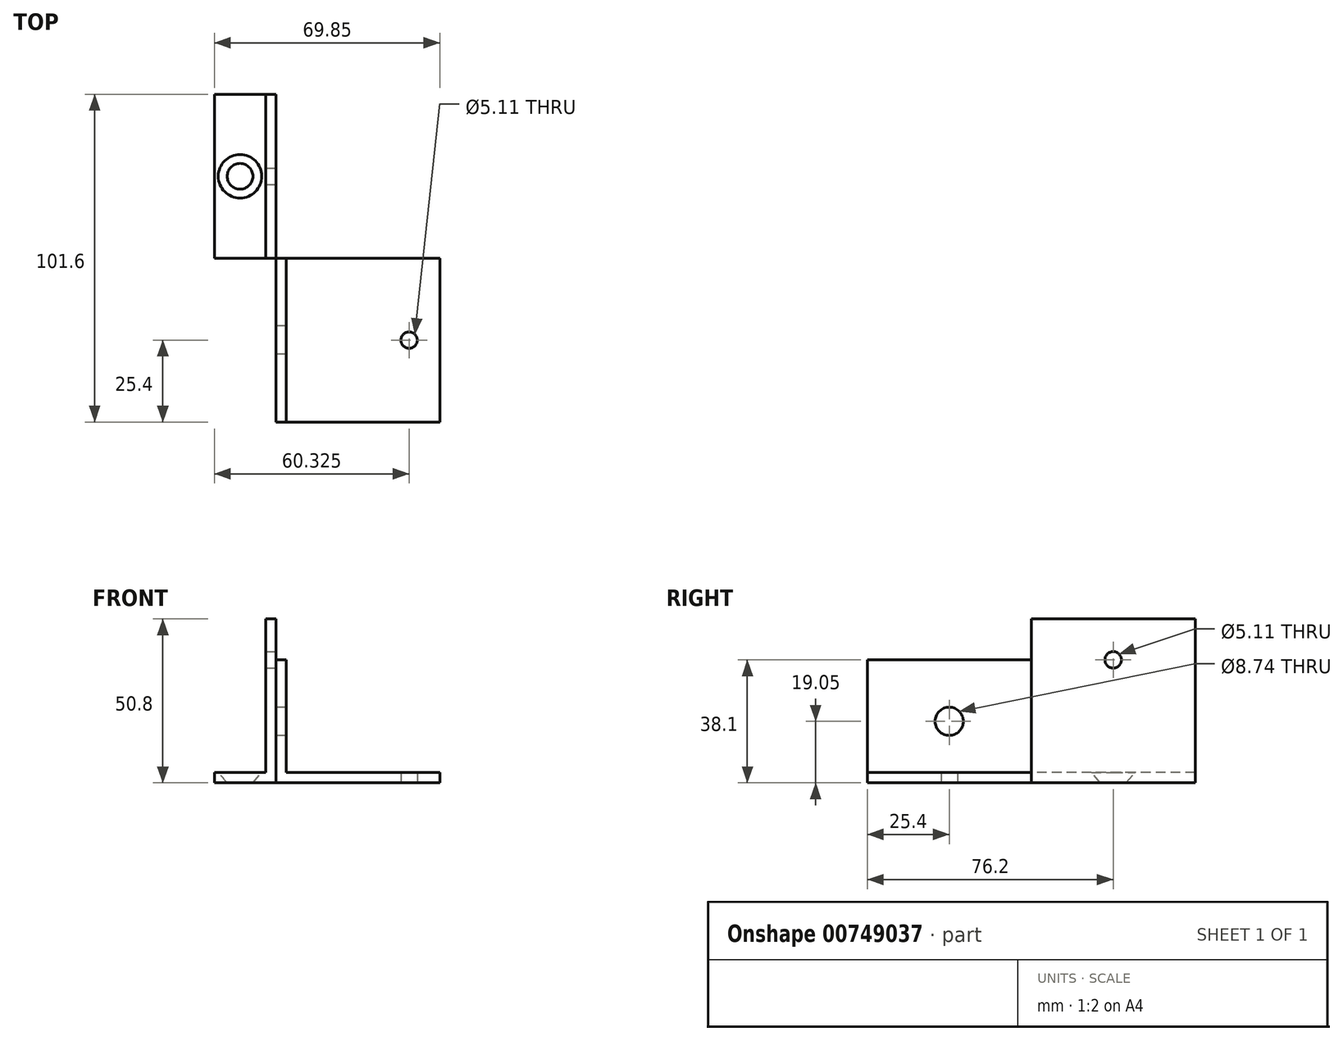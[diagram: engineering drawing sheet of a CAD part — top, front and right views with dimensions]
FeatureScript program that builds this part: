
annotation { "Feature Type Name" : "Feature", "Feature Type Description" : "" }
export const myFeature = defineFeature(function(context is Context, id is Id, definition is map)
    precondition{}
    {
        {
            var Q0;
            Q0=qCreatedBy(makeId("Front.planeOp"),FACE);
            var sketch = newSketch(context, id + "F0", { "sketchPlane" : qUnion([Q0])});
            skLineSegment(sketch, "E0", {"start": v(0, 0) * mm, "end": v(50.8, 0) * mm});
            skLineSegment(sketch, "E1", {"start": v(50.8, 0) * mm, "end": v(50.8, 3.18) * mm});
            skLineSegment(sketch, "E2", {"start": v(50.8, 3.18) * mm, "end": v(3.18, 3.18) * mm});
            skLineSegment(sketch, "E3", {"start": v(3.18, 3.17) * mm, "end": v(3.18, 50.8) * mm});
            skLineSegment(sketch, "E4", {"start": v(3.18, 50.8) * mm, "end": v(0, 50.8) * mm});
            skLineSegment(sketch, "E5", {"start": v(0, 50.8) * mm, "end": v(0, 0) * mm});
            skSolve(sketch);
        }
        {
            var Q0;
            Q0 = qSketchRegion(id + "F0", true);
            extrude(context, id + "F1", {"entities" : qUnion([Q0]), "depth" : 50.8 * mm, "offsetDistance" : 25.4 * mm});
        }
        {
            var Q0;
            Q0=makeQuery(id+"F1.opExtrude","SWEPT_FACE",FACE,{"disambiguationData":[OSD([sQuery(id+"F0.wireOp",EDGE,"E2")])]});
            var sketch = newSketch(context, id + "F2", { "sketchPlane" : qUnion([Q0])});
            skPoint(sketch, "E6", {"position": v(41.28, -25.4) * mm});
            skSolve(sketch);
        }
        {
            var Q0;
            Q0=sQuery(id+"F2.wireOp",VERTEX,"E6");
            var Q1;
            Q1=makeQuery(id+"F1.opExtrude","SWEPT_BODY",BODY,{"disambiguationData":[OSD([sQuery(id+"F0.wireOp",EDGE,"E0"),sQuery(id+"F0.wireOp",EDGE,"E1"),sQuery(id+"F0.wireOp",EDGE,"E2"),sQuery(id+"F0.wireOp",EDGE,"E3"),sQuery(id+"F0.wireOp",EDGE,"E4"),sQuery(id+"F0.wireOp",EDGE,"E5")])]});
            hole(context, id + "F3", {"style" : HoleStyle.SIMPLE, "endStyle" : HoleEndStyle.THROUGH, "standardTappedOrClearance" : lookupTablePath({ "standard" : "ANSI", "engagement" : "75%", "pitch" : "20 tpi", "size" : "1/4", "type" : "Tapped" }), "standardBlindInLast" : lookupTablePath({ "standard" : "ANSI", "fit" : "Normal", "engagement" : "75%", "pitch" : "20 tpi", "size" : "1/4", "type" : "Clearance & tapped" }), "holeDiameter" : 5.1 * mm, "majorDiameter" : 6.35 * mm, "showTappedDepth" : true, "isTappedThrough" : true, "tappedDepth" : 22.25 * mm, "tapClearance" : 3, "locations" : qUnion([Q0]), "scope" : qUnion([Q1])});
        }
        {
            var Q0;
            Q0=makeQuery(id+"F1.opExtrude","SWEPT_FACE",FACE,{"disambiguationData":[OSD([sQuery(id+"F0.wireOp",EDGE,"E3")])]});
            var sketch = newSketch(context, id + "F4", { "sketchPlane" : qUnion([Q0])});
            skPoint(sketch, "E7", {"position": v(-25.4, 19.05) * mm});
            skSolve(sketch);
        }
        {
            var Q0;
            Q0=sQuery(id+"F4.wireOp",VERTEX,"E7");
            var Q1;
            Q1=makeQuery(id+"F1.opExtrude","SWEPT_BODY",BODY,{"disambiguationData":[OSD([sQuery(id+"F0.wireOp",EDGE,"E0"),sQuery(id+"F0.wireOp",EDGE,"E1"),sQuery(id+"F0.wireOp",EDGE,"E2"),sQuery(id+"F0.wireOp",EDGE,"E3"),sQuery(id+"F0.wireOp",EDGE,"E4"),sQuery(id+"F0.wireOp",EDGE,"E5")])]});
            hole(context, id + "F5", {"style" : HoleStyle.SIMPLE, "endStyle" : HoleEndStyle.THROUGH, "standardTappedOrClearance" : lookupTablePath({ "fit" : "Normal (ASME)", "standard" : "ANSI", "size" : "5/16", "type" : "Clearance" }), "standardBlindInLast" : lookupTablePath({ "fit" : "Normal", "standard" : "ANSI", "engagement" : "75%", "pitch" : "18 tpi", "size" : "5/16", "type" : "Clearance & tapped" }), "holeDiameter" : 8.74 * mm, "majorDiameter" : 6.35 * mm, "isTappedThrough" : true, "tappedDepth" : 22.25 * mm, "tapClearance" : 3, "locations" : qUnion([Q0]), "scope" : qUnion([Q1])});
        }
        {
            var Q0;
            {var subQ0=sQuery(id+"F0.wireOp",EDGE,"E3");Q0=makeQuery(id+"F4.imprint","IMPRINT",FACE,{"disambiguationData":[TD([[makeQuery(id+"F4.imprint","IMPRINT",EDGE,{"derivedFrom":makeQuery(id+"F1.opExtrude","CAP_EDGE",EDGE,{"disambiguationData":[OSD([subQ0])],"isStart":true})}),1.0]])]});}
            var sketch = newSketch(context, id + "F6", { "sketchPlane" : qUnion([Q0])});
            skLineSegment(sketch, "E8.bottom", {"start": v(0, 78.68) * mm, "end": v(-68.85, 78.68) * mm});
            skLineSegment(sketch, "E8.top", {"start": v(0, 38.1) * mm, "end": v(-68.85, 38.1) * mm});
            skLineSegment(sketch, "E8.left", {"start": v(0, 78.68) * mm, "end": v(0, 38.1) * mm});
            skLineSegment(sketch, "E8.right", {"start": v(-68.85, 78.68) * mm, "end": v(-68.85, 38.1) * mm});
            skSolve(sketch);
        }
        {
            var Q0;
            Q0 = qSketchRegion(id + "F6", true);
            extrude(context, id + "F7", {"entities" : qUnion([Q0]), "operationType" : NewBodyOperationType.REMOVE, "oppositeDirection" : true, "depth" : 25.4 * mm, "offsetDistance" : 25.4 * mm});
        }
        {
            var Q0;
            Q0=qCreatedBy(makeId("Front.planeOp"),FACE);
            var sketch = newSketch(context, id + "F8", { "sketchPlane" : qUnion([Q0])});
            skLineSegment(sketch, "E9", {"start": v(0, 0) * mm, "end": v(0, 50.8) * mm});
            skLineSegment(sketch, "E10", {"start": v(0, 50.8) * mm, "end": v(-3.18, 50.8) * mm});
            skLineSegment(sketch, "E11", {"start": v(-3.18, 50.8) * mm, "end": v(-3.17, 3.18) * mm});
            skLineSegment(sketch, "E12", {"start": v(-3.18, 3.17) * mm, "end": v(-19.05, 3.17) * mm});
            skLineSegment(sketch, "E13", {"start": v(-19.05, 3.17) * mm, "end": v(-19.05, 0) * mm});
            skLineSegment(sketch, "E14", {"start": v(-19.05, 0) * mm, "end": v(0, 0) * mm});
            skSolve(sketch);
        }
        {
            var Q0;
            Q0 = qSketchRegion(id + "F8", true);
            extrude(context, id + "F9", {"entities" : qUnion([Q0]), "oppositeDirection" : true, "depth" : 50.8 * mm, "offsetDistance" : 25.4 * mm});
        }
        {
            var Q0;
            Q0=makeQuery(id+"F9.opExtrude","SWEPT_FACE",FACE,{"disambiguationData":[OSD([sQuery(id+"F8.wireOp",EDGE,"E12")])]});
            var sketch = newSketch(context, id + "F10", { "sketchPlane" : qUnion([Q0])});
            skPoint(sketch, "E15", {"position": v(-11.11, 25.4) * mm});
            skPoint(sketch, "E15.positionSnap0", {"position": v(-19.05, 25.4) * mm});
            skSolve(sketch);
        }
        {
            var Q0;
            Q0=sQuery(id+"F10.wireOp",VERTEX,"E15");
            var Q1;
            Q1=makeQuery(id+"F9.opExtrude","SWEPT_BODY",BODY,{"disambiguationData":[OSD([sQuery(id+"F8.wireOp",EDGE,"E9"),sQuery(id+"F8.wireOp",EDGE,"E10"),sQuery(id+"F8.wireOp",EDGE,"E11"),sQuery(id+"F8.wireOp",EDGE,"E12"),sQuery(id+"F8.wireOp",EDGE,"E13"),sQuery(id+"F8.wireOp",EDGE,"E14")])]});
            hole(context, id + "F11", {"style" : HoleStyle.C_SINK, "endStyle" : HoleEndStyle.THROUGH, "standardTappedOrClearance" : lookupTablePath({ "fit" : "Normal (ASME)", "standard" : "ANSI", "size" : "1/4", "type" : "Clearance" }), "standardBlindInLast" : lookupTablePath({ "fit" : "Normal", "standard" : "ANSI", "engagement" : "75%", "pitch" : "20 tpi", "size" : "1/4", "type" : "Clearance & tapped" }), "holeDiameter" : 7.14 * mm, "cSinkDiameter" : 13.5 * mm, "cSinkAngle" : 82 * degree, "majorDiameter" : 6.35 * mm, "isTappedThrough" : true, "tappedDepth" : 22.25 * mm, "tapClearance" : 3, "locations" : qUnion([Q0]), "scope" : qUnion([Q1])});
        }
        {
            var Q0;
            Q0=makeQuery(id+"F9.opExtrude","SWEPT_FACE",FACE,{"disambiguationData":[OSD([sQuery(id+"F8.wireOp",EDGE,"E11")])]});
            var sketch = newSketch(context, id + "F12", { "sketchPlane" : qUnion([Q0])});
            skPoint(sketch, "E16", {"position": v(-25.4, 38.1) * mm});
            skPoint(sketch, "E16.positionSnap0", {"position": v(-25.4, 50.8) * mm});
            skSolve(sketch);
        }
        {
            var Q0;
            Q0=sQuery(id+"F12.wireOp",VERTEX,"E16");
            var Q1;
            Q1=makeQuery(id+"F9.opExtrude","SWEPT_BODY",BODY,{"disambiguationData":[OSD([sQuery(id+"F8.wireOp",EDGE,"E9"),sQuery(id+"F8.wireOp",EDGE,"E10"),sQuery(id+"F8.wireOp",EDGE,"E11"),sQuery(id+"F8.wireOp",EDGE,"E12"),sQuery(id+"F8.wireOp",EDGE,"E13"),sQuery(id+"F8.wireOp",EDGE,"E14")])]});
            hole(context, id + "F13", {"style" : HoleStyle.SIMPLE, "endStyle" : HoleEndStyle.THROUGH, "standardTappedOrClearance" : lookupTablePath({ "standard" : "ANSI", "engagement" : "75%", "pitch" : "20 tpi", "size" : "1/4", "type" : "Tapped" }), "standardBlindInLast" : lookupTablePath({ "standard" : "ANSI", "fit" : "Normal", "engagement" : "75%", "pitch" : "20 tpi", "size" : "1/4", "type" : "Clearance & tapped" }), "holeDiameter" : 5.1 * mm, "majorDiameter" : 6.35 * mm, "showTappedDepth" : true, "tappedDepth" : 22.25 * mm, "tapClearance" : 3, "locations" : qUnion([Q0]), "scope" : qUnion([Q1])});
        }
    });
